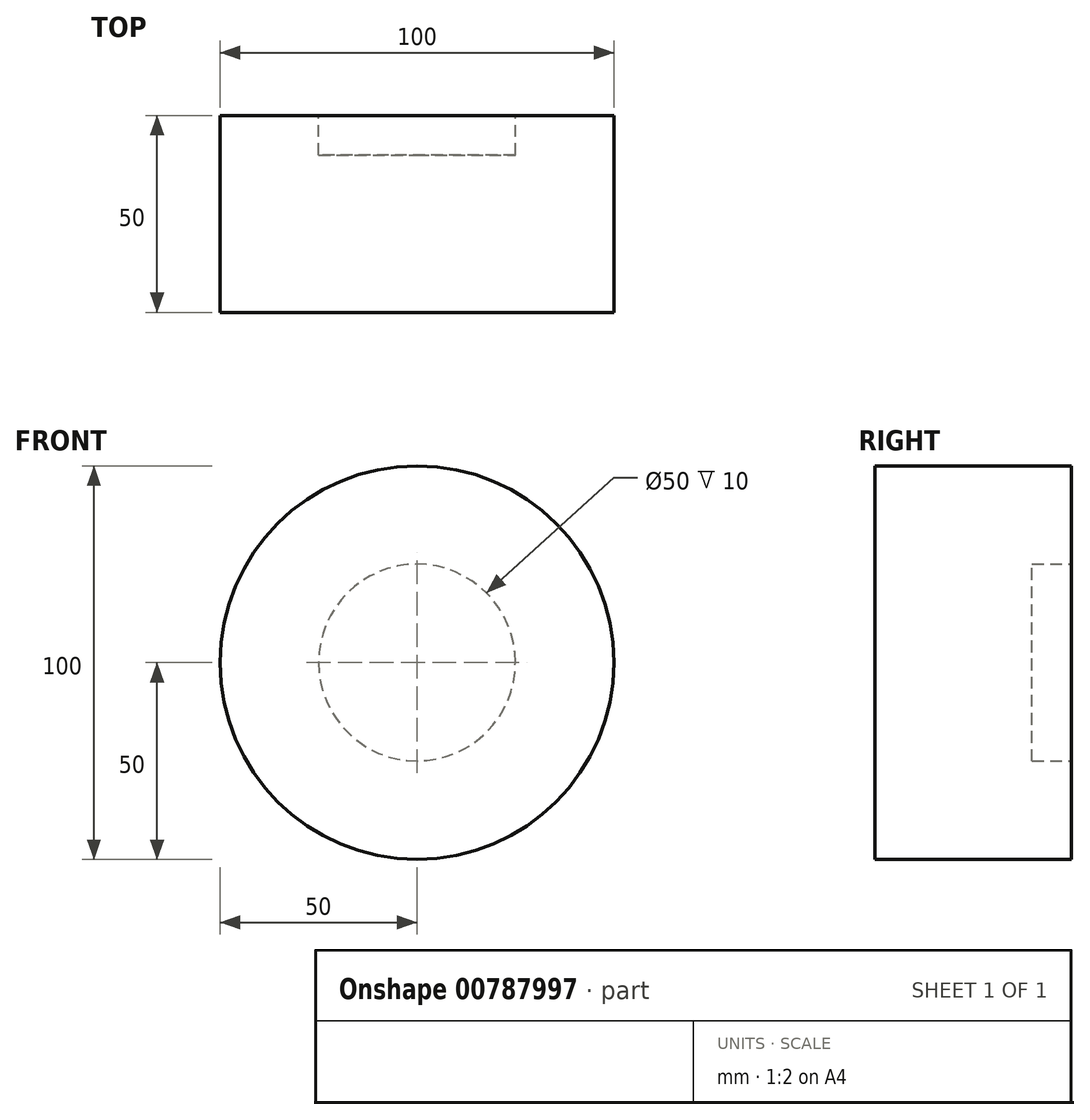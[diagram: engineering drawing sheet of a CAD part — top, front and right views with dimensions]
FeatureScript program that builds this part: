
annotation { "Feature Type Name" : "Feature", "Feature Type Description" : "" }
export const myFeature = defineFeature(function(context is Context, id is Id, definition is map)
    precondition{}
    {
        {
            var Q0;
            Q0=qCreatedBy(makeId("Front.planeOp"),FACE);
            var sketch = newSketch(context, id + "F0", { "sketchPlane" : qUnion([Q0])});
            skCircle(sketch, "E0", {"center": v(0, 0) * mm, "radius": 25 * mm});
            skLineSegment(sketch, "E1", {"start": v(0, 25) * mm, "end": v(0, 31.57) * mm});
            skLineSegment(sketch, "E2", {"start": v(-30.15, 0) * mm, "end": v(30.06, 0) * mm, "construction": true});
            skLineSegment(sketch, "E3", {"start": v(0, 28.29) * mm, "end": v(0, -28.75) * mm, "construction": true});
            skCircle(sketch, "E4", {"center": v(0, 0) * mm, "radius": 50 * mm});
            skSolve(sketch);
        }
        {
            var Q0;
            Q0 = qSketchRegion(id + "F0", true);
            var Q1;
            Q1=makeQuery(id+"F0.imprint","IMPRINT",FACE,{"disambiguationData":[TD([[makeQuery(id+"F0.imprint","IMPRINT",EDGE,{"derivedFrom":sQuery(id+"F0.wireOp",EDGE,"E0")}),1.0]])]});
            extrude(context, id + "F1", {"entities" : qUnion([Q0, Q1]), "depth" : 50 * mm, "offsetDistance" : 25 * mm});
        }
        {
            var Q0;
            Q0=qCreatedBy(makeId("Front.planeOp"),FACE);
            var sketch = newSketch(context, id + "F2", { "sketchPlane" : qUnion([Q0])});
            skCircle(sketch, "E5", {"center": v(0, 0) * mm, "radius": 25 * mm});
            skSolve(sketch);
        }
        {
            var Q0;
            Q0 = qSketchRegion(id + "F2", true);
            var Q1;
            Q1=makeQuery(id+"F2.imprint","IMPRINT",FACE,{"disambiguationData":[TD([[makeQuery(id+"F2.imprint","IMPRINT",EDGE,{"derivedFrom":sQuery(id+"F2.wireOp",EDGE,"E5")}),1.0]])]});
            extrude(context, id + "F3", {"entities" : qUnion([Q0, Q1]), "operationType" : NewBodyOperationType.REMOVE, "depth" : 10 * mm, "offsetDistance" : 25 * mm});
        }
    });
